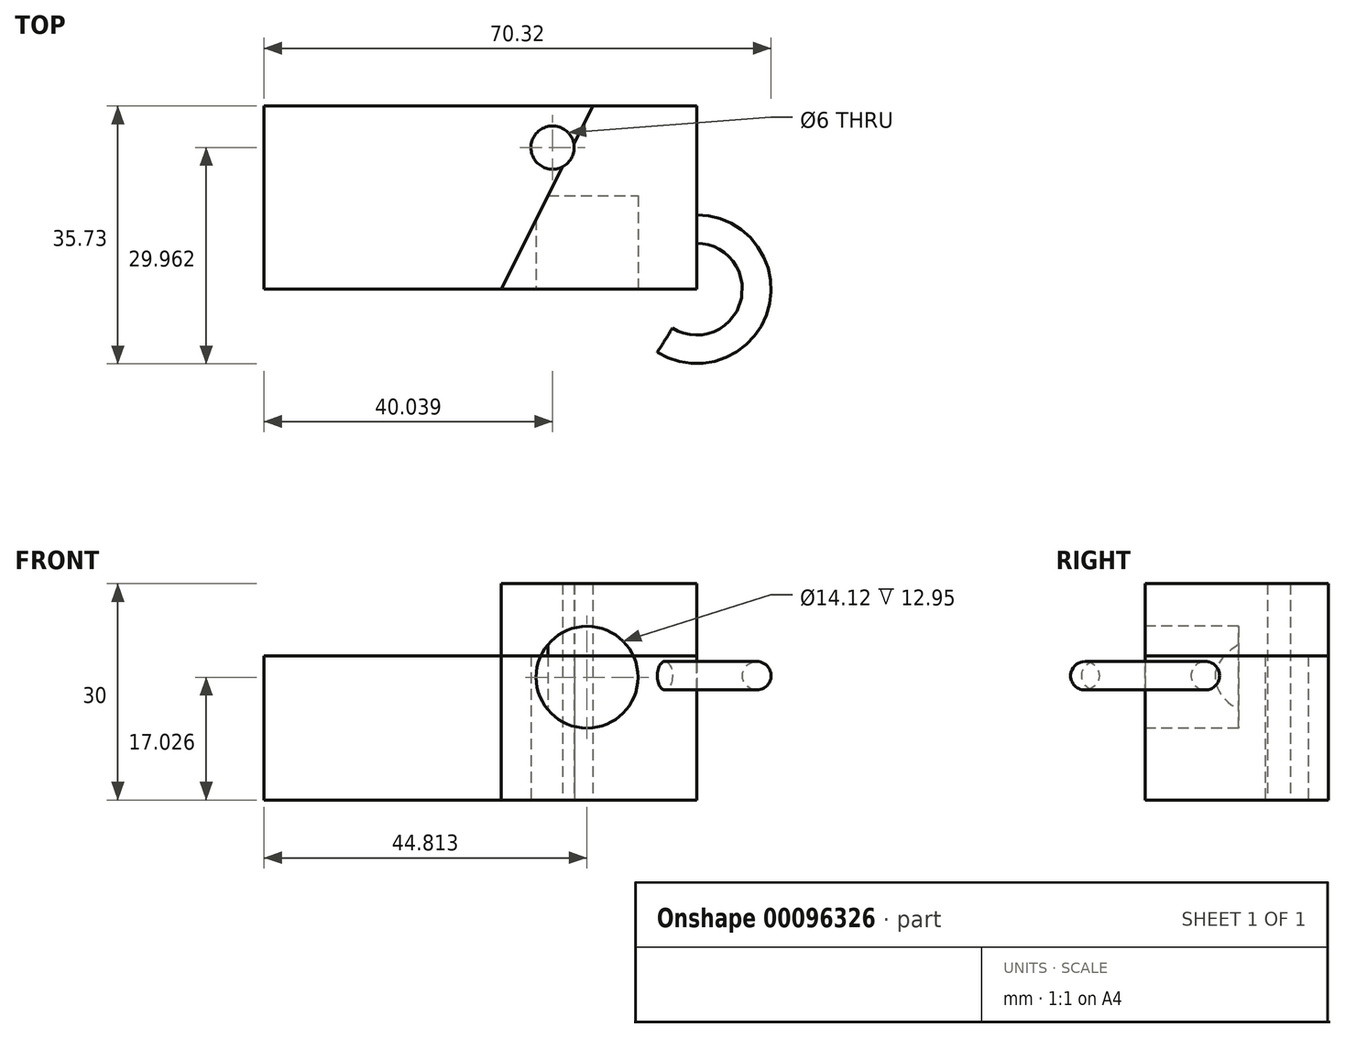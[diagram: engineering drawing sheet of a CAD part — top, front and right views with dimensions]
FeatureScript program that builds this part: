
annotation { "Feature Type Name" : "Feature", "Feature Type Description" : "" }
export const myFeature = defineFeature(function(context is Context, id is Id, definition is map)
    precondition{}
    {
        {
            var Q0;
            Q0=qCreatedBy(makeId("Top.planeOp"),FACE);
            var sketch = newSketch(context, id + "F0", { "sketchPlane" : qUnion([Q0])});
            skLineSegment(sketch, "E0.bottom", {"start": v(-68.54, 1.5) * mm, "end": v(-8.54, 1.5) * mm});
            skLineSegment(sketch, "E0.top", {"start": v(-68.54, -23.9) * mm, "end": v(-8.54, -23.9) * mm});
            skLineSegment(sketch, "E0.left", {"start": v(-68.54, 1.5) * mm, "end": v(-68.54, -23.9) * mm});
            skLineSegment(sketch, "E0.right", {"start": v(-8.54, 1.5) * mm, "end": v(-8.54, -23.9) * mm});
            skCircle(sketch, "E1", {"center": v(-28.5, -4.27) * mm, "radius": 3 * mm});
            skLineSegment(sketch, "E2.bottom", {"start": v(1.46, 40.57) * mm, "end": v(53.28, 40.57) * mm});
            skLineSegment(sketch, "E2.top", {"start": v(1.46, 17.25) * mm, "end": v(53.28, 17.25) * mm});
            skLineSegment(sketch, "E2.left", {"start": v(1.46, 40.57) * mm, "end": v(1.46, 17.25) * mm});
            skLineSegment(sketch, "E2.right", {"start": v(53.28, 40.57) * mm, "end": v(53.28, 17.25) * mm});
            skLineSegment(sketch, "E3", {"start": v(-16.82, 13.61) * mm, "end": v(-38.08, -28.74) * mm});
            skSolve(sketch);
        }
        {
            var Q0;
            {var subQ6=sQuery(id+"F0.wireOp",EDGE,"E0.right");Q0=makeQuery(id+"F0.imprint","IMPRINT",FACE,{"disambiguationData":[TD([[makeQuery(id+"F0.imprint","IMPRINT",EDGE,{"derivedFrom":subQ6}),-1.0]])]});}
            extrude(context, id + "F1", {"entities" : qUnion([Q0]), "depth" : 30 * mm});
        }
        {
            var Q0;
            Q0=makeQuery(id+"F1.opExtrude","SWEPT_FACE",FACE,{"disambiguationData":[OSD([sQuery(id+"F0.wireOp",EDGE,"E0.top")])]});
            var sketch = newSketch(context, id + "F2", { "sketchPlane" : qUnion([Q0])});
            skCircle(sketch, "E4", {"center": v(-23.73, 17.03) * mm, "radius": 7.06 * mm});
            skSolve(sketch);
        }
        {
            var Q0;
            Q0=makeQuery(id+"F2.imprint","IMPRINT",FACE,{"disambiguationData":[TD([[makeQuery(id+"F2.imprint","IMPRINT",EDGE,{"derivedFrom":sQuery(id+"F2.wireOp",EDGE,"E4")}),1.0]])]});
            extrude(context, id + "F3", {"entities" : qUnion([Q0]), "operationType" : NewBodyOperationType.REMOVE, "oppositeDirection" : true, "depth" : 12.95 * mm});
        }
        {
            var Q0;
            Q0=makeQuery(id+"F1.opExtrude","SWEPT_FACE",FACE,{"disambiguationData":[OSD([sQuery(id+"F0.wireOp",EDGE,"E0.right")])]});
            var sketch = newSketch(context, id + "F4", { "sketchPlane" : qUnion([Q0])});
            skCircle(sketch, "E5", {"center": v(-15.55, 17.23) * mm, "radius": 1.98 * mm});
            skSolve(sketch);
        }
        {
            var Q0;
            Q0=makeQuery(id+"F4.imprint","IMPRINT",FACE,{"disambiguationData":[TD([[makeQuery(id+"F4.imprint","IMPRINT",EDGE,{"derivedFrom":sQuery(id+"F4.wireOp",EDGE,"E5")}),1.0]])]});
            var Q1;
            Q1=makeQuery(id+"F1.opExtrude","SWEPT_EDGE",EDGE,{"disambiguationData":[OSD([sQuery(id+"F0.wireOp",EDGE,"E0.top"),sQuery(id+"F0.wireOp",EDGE,"E0.right")])]});
            revolve(context, id + "F5", {"operationType" : NewBodyOperationType.ADD, "entities" : qUnion([Q0]), "axis" : qUnion([Q1]), "revolveType" : RevolveType.ONE_DIRECTION, "angle" : 211.83 * degree});
        }
        {
            var Q0;
            Q0=makeQuery(id+"F0.imprint","IMPRINT",FACE,{"disambiguationData":[TD([[makeQuery(id+"F0.imprint","IMPRINT",EDGE,{"derivedFrom":sQuery(id+"F0.wireOp",EDGE,"E0.top")}),1.0]])]});
            extrude(context, id + "F6", {"entities" : qUnion([Q0]), "depth" : 20 * mm});
        }
    });
